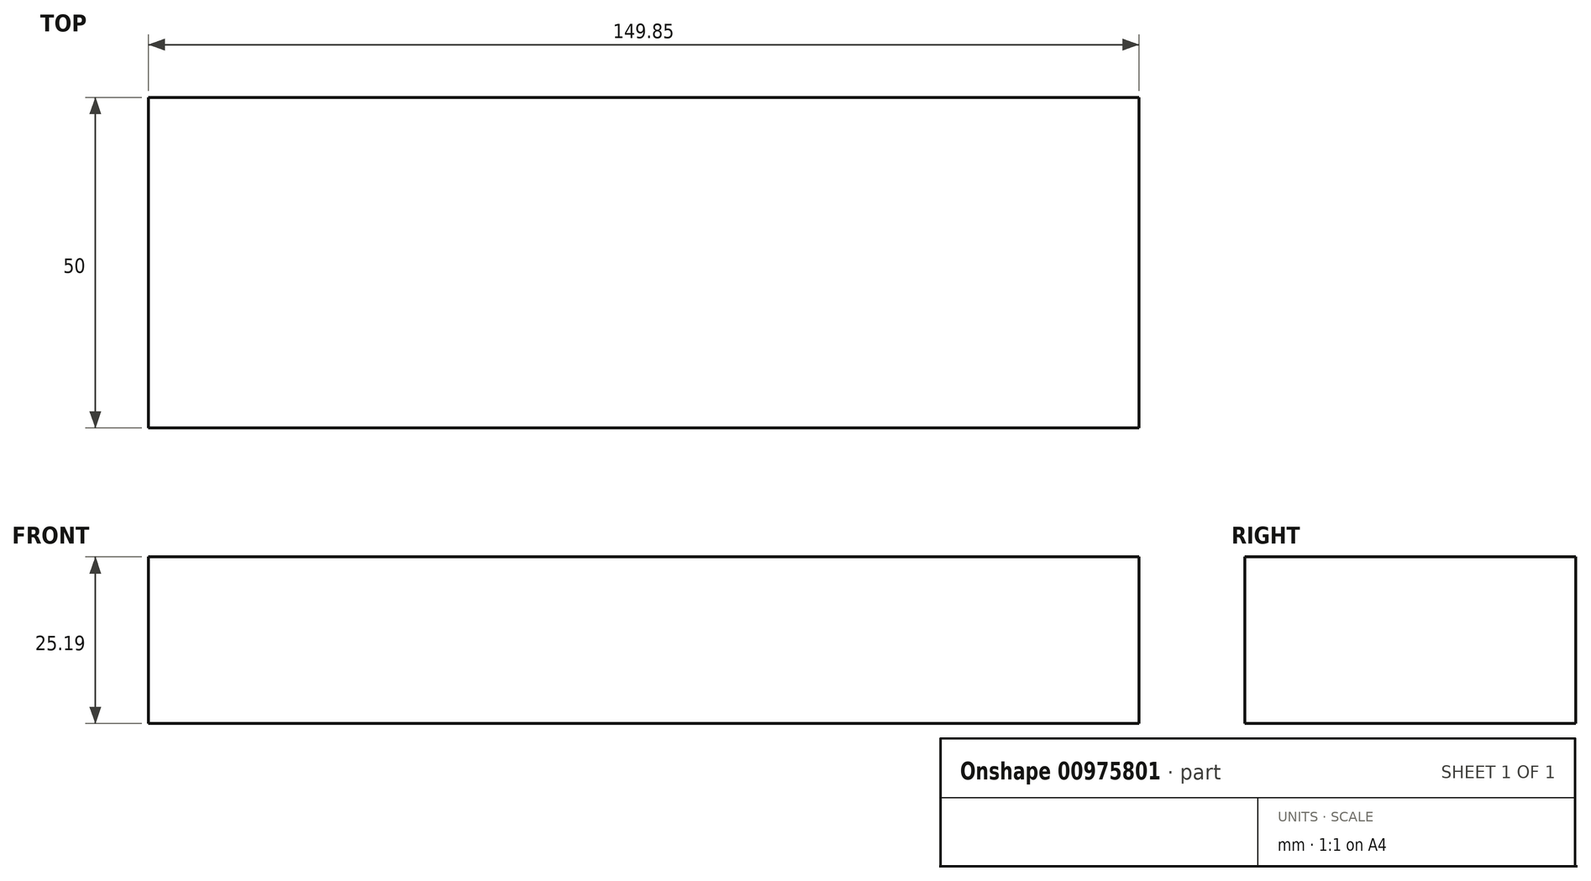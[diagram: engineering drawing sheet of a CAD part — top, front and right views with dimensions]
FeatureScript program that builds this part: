
annotation { "Feature Type Name" : "Feature", "Feature Type Description" : "" }
export const myFeature = defineFeature(function(context is Context, id is Id, definition is map)
    precondition{}
    {
        {
            var Q0;
            Q0=qCreatedBy(makeId("Front.planeOp"),FACE);
            var sketch = newSketch(context, id + "F0", { "sketchPlane" : qUnion([Q0])});
            skLineSegment(sketch, "E0.bottom", {"start": v(-75.4, 5.58) * mm, "end": v(74.45, 5.58) * mm});
            skLineSegment(sketch, "E0.top", {"start": v(-75.4, -19.6) * mm, "end": v(74.45, -19.6) * mm});
            skLineSegment(sketch, "E0.left", {"start": v(-75.4, 5.58) * mm, "end": v(-75.4, -19.6) * mm});
            skLineSegment(sketch, "E0.right", {"start": v(74.45, 5.58) * mm, "end": v(74.45, -19.6) * mm});
            skSolve(sketch);
        }
        {
            var Q0;
            Q0=makeQuery(id+"F0.imprint","IMPRINT",FACE,{"disambiguationData":[TD([[makeQuery(id+"F0.imprint","IMPRINT",EDGE,{"derivedFrom":sQuery(id+"F0.wireOp",EDGE,"E0.bottom")}),-1.0]])]});
            extrude(context, id + "F1", {"entities" : qUnion([Q0]), "depth" : 50 * mm, "offsetDistance" : 25 * mm});
        }
    });
